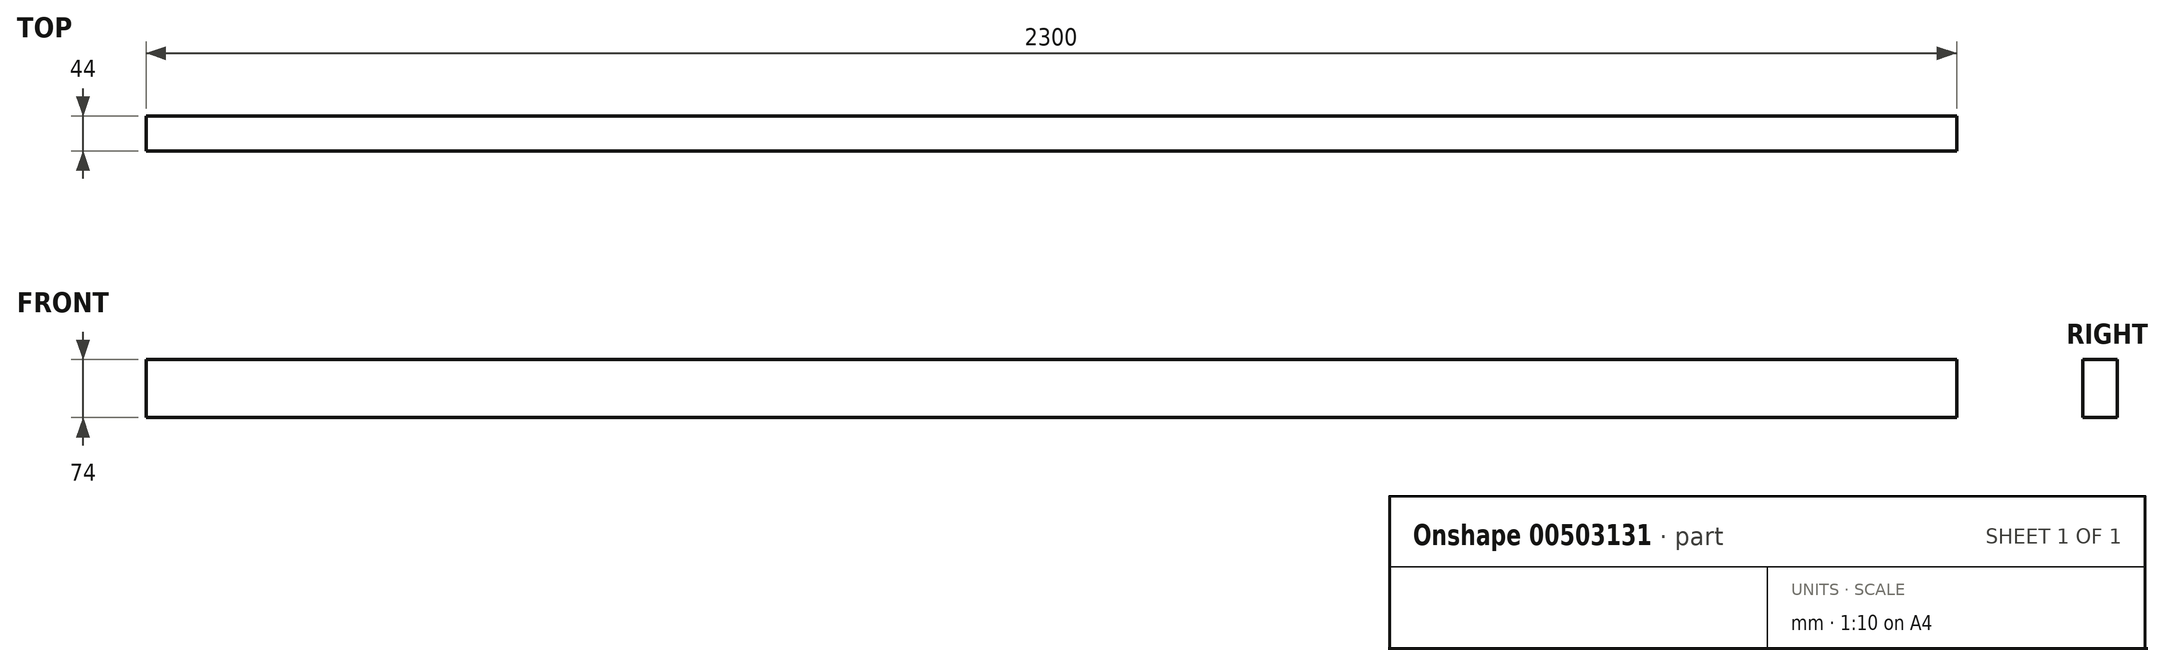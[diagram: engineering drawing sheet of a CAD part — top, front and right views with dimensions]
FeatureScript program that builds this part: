
annotation { "Feature Type Name" : "Feature", "Feature Type Description" : "" }
export const myFeature = defineFeature(function(context is Context, id is Id, definition is map)
    precondition{}
    {
        {
            var Q0;
            Q0=qCreatedBy(makeId("Front.planeOp"),FACE);
            var sketch = newSketch(context, id + "F0", { "sketchPlane" : qUnion([Q0])});
            skLineSegment(sketch, "E0.bottom", {"start": v(-410.5, 34.9) * mm, "end": v(1889.5, 34.9) * mm});
            skLineSegment(sketch, "E0.top", {"start": v(-410.5, -39.1) * mm, "end": v(1889.5, -39.1) * mm});
            skLineSegment(sketch, "E0.left", {"start": v(-410.5, 34.9) * mm, "end": v(-410.5, -39.1) * mm});
            skLineSegment(sketch, "E0.right", {"start": v(1889.5, 34.9) * mm, "end": v(1889.5, -39.1) * mm});
            skSolve(sketch);
        }
        {
            var Q0;
            Q0=makeQuery(id+"F0.imprint","IMPRINT",FACE,{"disambiguationData":[TD([[makeQuery(id+"F0.imprint","IMPRINT",EDGE,{"derivedFrom":sQuery(id+"F0.wireOp",EDGE,"E0.bottom")}),-1.0]])]});
            extrude(context, id + "F1", {"entities" : qUnion([Q0]), "depth" : 44 * mm, "offsetDistance" : 25 * mm});
        }
    });
